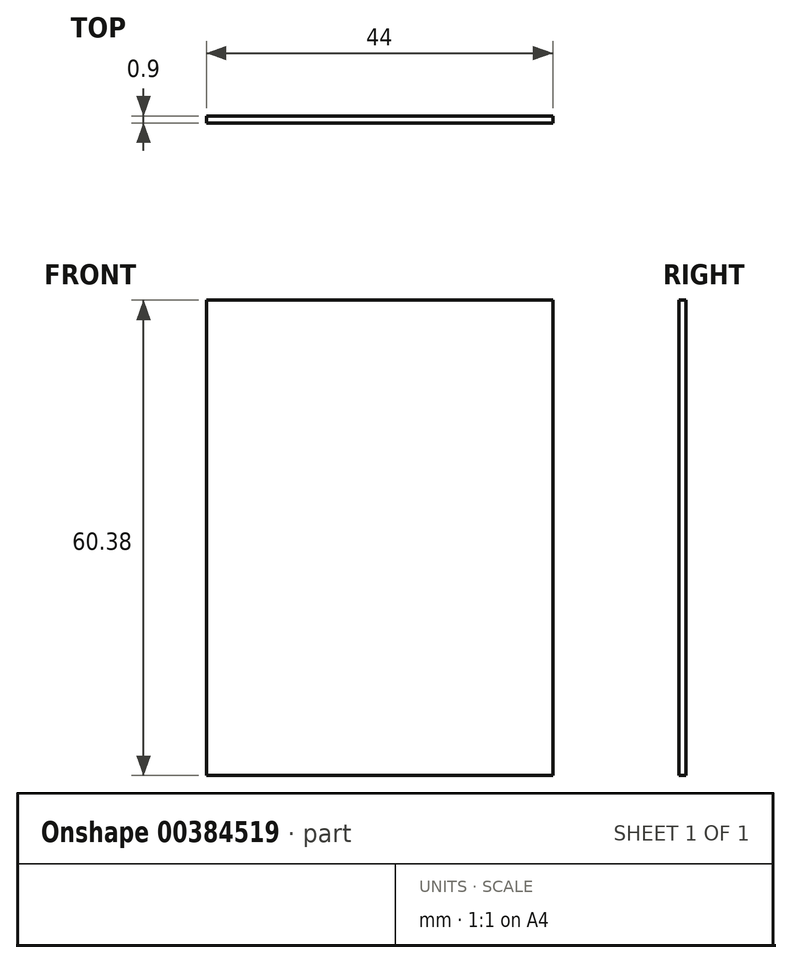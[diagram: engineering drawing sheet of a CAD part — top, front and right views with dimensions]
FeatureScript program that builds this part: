
annotation { "Feature Type Name" : "Feature", "Feature Type Description" : "" }
export const myFeature = defineFeature(function(context is Context, id is Id, definition is map)
    precondition{}
    {
        {
            var Q0;
            Q0=qCreatedBy(makeId("Front.planeOp"),FACE);
            var sketch = newSketch(context, id + "F0", { "sketchPlane" : qUnion([Q0])});
            skLineSegment(sketch, "E0.bottom", {"start": v(-17.06, 30.98) * mm, "end": v(26.94, 30.98) * mm});
            skLineSegment(sketch, "E0.top", {"start": v(-17.06, -29.4) * mm, "end": v(26.94, -29.4) * mm});
            skLineSegment(sketch, "E0.left", {"start": v(-17.06, 30.98) * mm, "end": v(-17.06, -29.4) * mm});
            skLineSegment(sketch, "E0.right", {"start": v(26.94, 30.98) * mm, "end": v(26.94, -29.4) * mm});
            skSolve(sketch);
        }
        {
            var Q0;
            Q0=makeQuery(id+"F0.imprint","IMPRINT",FACE,{"disambiguationData":[TD([[makeQuery(id+"F0.imprint","IMPRINT",EDGE,{"derivedFrom":sQuery(id+"F0.wireOp",EDGE,"E0.bottom")}),-1.0]])]});
            extrude(context, id + "F1", {"entities" : qUnion([Q0]), "depth" : 0.9 * mm});
        }
    });
